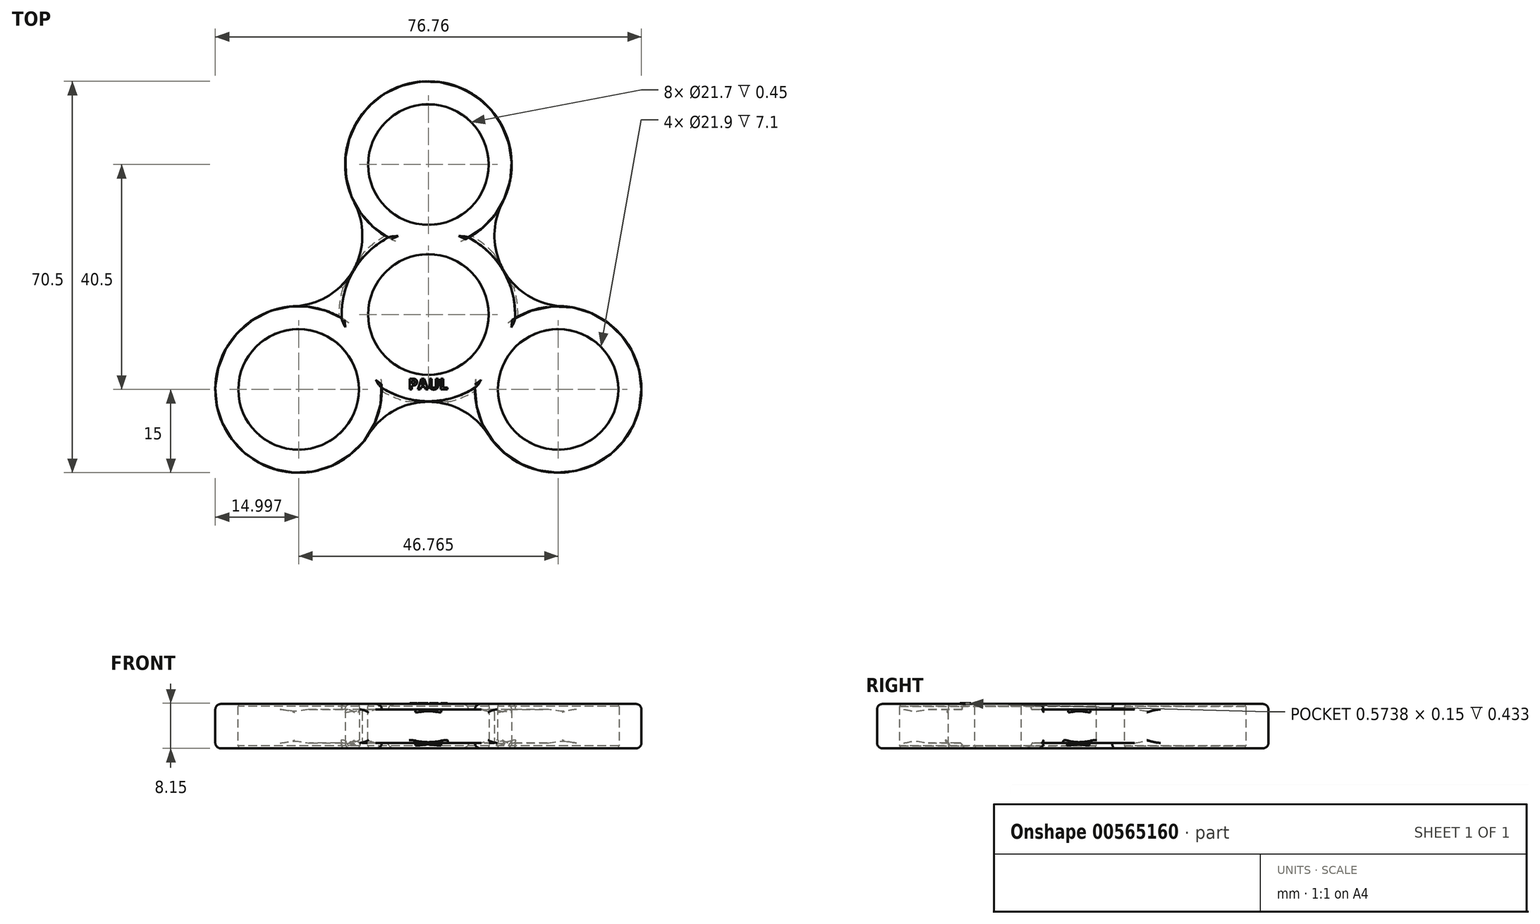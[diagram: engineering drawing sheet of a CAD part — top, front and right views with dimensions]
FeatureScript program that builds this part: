
annotation { "Feature Type Name" : "Feature", "Feature Type Description" : "" }
export const myFeature = defineFeature(function(context is Context, id is Id, definition is map)
    precondition{}
    {
        {
            var Q0;
            Q0=qCreatedBy(makeId("Top.planeOp"),FACE);
            var sketch = newSketch(context, id + "F0", { "sketchPlane" : qUnion([Q0])});
            skCircle(sketch, "E0", {"center": v(0, 0) * mm, "radius": 10.85 * mm});
            skCircle(sketch, "E1", {"center": v(0, 27) * mm, "radius": 10.85 * mm});
            skCircle(sketch, "E2.1.0", {"center": v(-23.38, -13.5) * mm, "radius": 10.85 * mm});
            skCircle(sketch, "E2.2.0", {"center": v(23.38, -13.5) * mm, "radius": 10.85 * mm});
            skArc(sketch, "E3", {"start": v(7.22, 13.85) * mm, "mid": v(0, 42) * mm, "end": v(-7.22, 13.85) * mm});
            skArc(sketch, "E4.1.0", {"start": v(8.39, -13.18) * mm, "mid": v(36.37, -21) * mm, "end": v(15.61, -0.67) * mm});
            skArc(sketch, "E4.2.0", {"start": v(-15.61, -0.67) * mm, "mid": v(-36.37, -21) * mm, "end": v(-8.39, -13.18) * mm});
            skArc(sketch, "E5", {"start": v(-8.39, -13.18) * mm, "mid": v(0, -15.62) * mm, "end": v(8.39, -13.18) * mm});
            skArc(sketch, "E6", {"start": v(-24.08, 1.48) * mm, "mid": v(-13.61, 7.86) * mm, "end": v(-13.33, 20.12) * mm});
            skArc(sketch, "E7", {"start": v(10.76, -21.6) * mm, "mid": v(0, -15.72) * mm, "end": v(-10.76, -21.6) * mm});
            skArc(sketch, "E8", {"start": v(13.33, 20.12) * mm, "mid": v(13.61, 7.86) * mm, "end": v(24.08, 1.48) * mm});
            skPoint(sketch, "E9.orphan", {"position": v(-13, 34.5) * mm});
            skPoint(sketch, "E10.orphan", {"position": v(-36.37, -6) * mm});
            skPoint(sketch, "E11.orphan", {"position": v(13, 34.5) * mm});
            skPoint(sketch, "E12.2.0.start.orphan", {"position": v(36.37, -6) * mm});
            skPoint(sketch, "E13.orphan", {"position": v(23.38, -28.5) * mm});
            skPoint(sketch, "E12.1.0.start.orphan", {"position": v(-23.38, -28.5) * mm});
            skArc(sketch, "E14.trimOffspring", {"start": v(15.61, -0.67) * mm, "mid": v(13.53, 7.81) * mm, "end": v(7.22, 13.85) * mm});
            skArc(sketch, "E15.trimOffspring", {"start": v(-7.22, 13.85) * mm, "mid": v(-13.53, 7.81) * mm, "end": v(-15.61, -0.67) * mm});
            skCircle(sketch, "E16", {"center": v(23.38, -13.5) * mm, "radius": 10.95 * mm});
            skCircle(sketch, "E17", {"center": v(-23.38, -13.5) * mm, "radius": 10.95 * mm});
            skCircle(sketch, "E18", {"center": v(0, 0) * mm, "radius": 10.95 * mm});
            skCircle(sketch, "E19", {"center": v(0, 27) * mm, "radius": 10.95 * mm});
            skSolve(sketch);
        }
        {
            var Q0;
            Q0=makeQuery(id+"F0.imprint","IMPRINT",FACE,{"disambiguationData":[TD([[makeQuery(id+"F0.imprint","IMPRINT",EDGE,{"derivedFrom":sQuery(id+"F0.wireOp",EDGE,"E2.1.0")}),-1.0]])]});
            var Q1;
            Q1=makeQuery(id+"F0.imprint","IMPRINT",FACE,{"disambiguationData":[TD([[makeQuery(id+"F0.imprint","IMPRINT",EDGE,{"derivedFrom":sQuery(id+"F0.wireOp",EDGE,"E0")}),-1.0]])]});
            var Q2;
            Q2=makeQuery(id+"F0.imprint","IMPRINT",FACE,{"disambiguationData":[TD([[makeQuery(id+"F0.imprint","IMPRINT",EDGE,{"derivedFrom":sQuery(id+"F0.wireOp",EDGE,"E1")}),-1.0]])]});
            var Q3;
            {var subQ0=sQuery(id+"F0.wireOp",EDGE,"E3");var subQ1=sQuery(id+"F0.wireOp",EDGE,"KJlQqC9l-gusD-toYh-YzLE-zyJcLNbmcpUm");var subQ2=makeQuery(id+"F0.imprint","INTERSECT",VERTEX,{"derivedFrom":[subQ1,subQ0]});Q3=makeQuery(id+"F0.imprint","IMPRINT",FACE,{"disambiguationData":[TD([[makeQuery(id+"F0.imprint","IMPRINT",EDGE,{"disambiguationData":[TD([[subQ2,1.0]])],"derivedFrom":subQ1}),1.0]])]});}
            var Q4;
            {var subQ0=sQuery(id+"F0.wireOp",EDGE,"E3");var subQ1=sQuery(id+"F0.wireOp",EDGE,"KJlQqC9l-gusD-toYh-YzLE-zyJcLNbmcpUm");var subQ2=makeQuery(id+"F0.imprint","INTERSECT",VERTEX,{"derivedFrom":[subQ1,subQ0]});Q4=makeQuery(id+"F0.imprint","IMPRINT",FACE,{"disambiguationData":[TD([[makeQuery(id+"F0.imprint","IMPRINT",EDGE,{"disambiguationData":[TD([[subQ2,1.0]])],"derivedFrom":subQ1}),-1.0]])]});}
            var Q5;
            {var subQ0=sQuery(id+"F0.wireOp",EDGE,"E5");var subQ1=sQuery(id+"F0.wireOp",EDGE,"E4.2.0");var subQ2=makeQuery(id+"F0.imprint","INTERSECT",VERTEX,{"disambiguationData":[OD(0.0)],"derivedFrom":[subQ1,subQ0]});Q5=makeQuery(id+"F0.imprint","IMPRINT",FACE,{"disambiguationData":[TD([[makeQuery(id+"F0.imprint","IMPRINT",EDGE,{"disambiguationData":[TD([[subQ2,-1.0]])],"derivedFrom":subQ1}),1.0]])]});}
            var Q6;
            Q6=makeQuery(id+"F0.imprint","IMPRINT",FACE,{"disambiguationData":[TD([[makeQuery(id+"F0.imprint","IMPRINT",EDGE,{"derivedFrom":sQuery(id+"F0.wireOp",EDGE,"E2.2.0")}),-1.0]])]});
            var Q7;
            {var subQ0=sQuery(id+"F0.wireOp",EDGE,"E5");var subQ1=sQuery(id+"F0.wireOp",EDGE,"E4.1.0");var subQ2=makeQuery(id+"F0.imprint","INTERSECT",VERTEX,{"disambiguationData":[OD(0.0)],"derivedFrom":[subQ1,subQ0]});Q7=makeQuery(id+"F0.imprint","IMPRINT",FACE,{"disambiguationData":[TD([[makeQuery(id+"F0.imprint","IMPRINT",EDGE,{"disambiguationData":[TD([[subQ2,-1.0]])],"derivedFrom":subQ1}),1.0]])]});}
            extrude(context, id + "F1", {"entities" : qUnion([Q0, Q1, Q2, Q3, Q4, Q5, Q6, Q7]), "endBound" : BoundingType.SYMMETRIC, "depth" : 8 * mm, "offsetDistance" : 25 * mm});
        }
        {
            var Q0;
            {var subQ0=sQuery(id+"F0.wireOp",EDGE,"E7");Q0=makeQuery(id+"F0.imprint","IMPRINT",FACE,{"disambiguationData":[TD([[makeQuery(id+"F0.imprint","IMPRINT",EDGE,{"derivedFrom":subQ0}),-1.0]])]});}
            var Q1;
            {var subQ0=sQuery(id+"F0.wireOp",EDGE,"E6");Q1=makeQuery(id+"F0.imprint","IMPRINT",FACE,{"disambiguationData":[TD([[makeQuery(id+"F0.imprint","IMPRINT",EDGE,{"derivedFrom":subQ0}),-1.0]])]});}
            var Q2;
            {var subQ0=sQuery(id+"F0.wireOp",EDGE,"E8");Q2=makeQuery(id+"F0.imprint","IMPRINT",FACE,{"disambiguationData":[TD([[makeQuery(id+"F0.imprint","IMPRINT",EDGE,{"derivedFrom":subQ0}),-1.0]])]});}
            extrude(context, id + "F2", {"entities" : qUnion([Q0, Q1, Q2]), "operationType" : NewBodyOperationType.ADD, "endBound" : BoundingType.SYMMETRIC, "depth" : 6 * mm, "offsetDistance" : 25 * mm});
        }
        {
            var Q0;
            Q0=makeQuery(id+"F1.opExtrude","CAP_EDGE",EDGE,{"disambiguationData":[OSD([sQuery(id+"F0.wireOp",EDGE,"E15.trimOffspring")])],"isStart":true});
            var Q1;
            Q1=makeQuery(id+"F2.opExtrude","CAP_EDGE",EDGE,{"disambiguationData":[OSD([sQuery(id+"F0.wireOp",EDGE,"E15.trimOffspring")])],"isStart":true});
            var Q2;
            Q2=makeQuery(id+"F1.opExtrude","CAP_EDGE",EDGE,{"disambiguationData":[OSD([sQuery(id+"F0.wireOp",EDGE,"E5")])],"isStart":true});
            var Q3;
            Q3=makeQuery(id+"F2.opExtrude","CAP_EDGE",EDGE,{"disambiguationData":[OSD([sQuery(id+"F0.wireOp",EDGE,"E5")])],"isStart":true});
            var Q4;
            Q4=makeQuery(id+"F1.opExtrude","CAP_EDGE",EDGE,{"disambiguationData":[OSD([sQuery(id+"F0.wireOp",EDGE,"E14.trimOffspring")])],"isStart":true});
            var Q5;
            Q5=makeQuery(id+"F2.opExtrude","CAP_EDGE",EDGE,{"disambiguationData":[OSD([sQuery(id+"F0.wireOp",EDGE,"E14.trimOffspring")])],"isStart":true});
            fillet(context, id + "F3", {"entities" : qUnion([Q0, Q1, Q2, Q3, Q4, Q5]), "radius" : 0.5 * mm, "rho" : 0.5, "crossSection" : FilletCrossSection.CONIC, "allowEdgeOverflow" : false});
        }
        {
            var Q0;
            Q0=makeQuery(id+"F1.opExtrude","CAP_EDGE",EDGE,{"disambiguationData":[OSD([sQuery(id+"F0.wireOp",EDGE,"E5")])],"isStart":false});
            var Q1;
            Q1=makeQuery(id+"F2.opExtrude","CAP_EDGE",EDGE,{"disambiguationData":[OSD([sQuery(id+"F0.wireOp",EDGE,"E5")])],"isStart":false});
            var Q2;
            Q2=makeQuery(id+"F1.opExtrude","CAP_EDGE",EDGE,{"disambiguationData":[OSD([sQuery(id+"F0.wireOp",EDGE,"E14.trimOffspring")])],"isStart":false});
            var Q3;
            Q3=makeQuery(id+"F2.opExtrude","CAP_EDGE",EDGE,{"disambiguationData":[OSD([sQuery(id+"F0.wireOp",EDGE,"E14.trimOffspring")])],"isStart":false});
            var Q4;
            Q4=makeQuery(id+"F1.opExtrude","CAP_EDGE",EDGE,{"disambiguationData":[OSD([sQuery(id+"F0.wireOp",EDGE,"E15.trimOffspring")])],"isStart":false});
            var Q5;
            Q5=makeQuery(id+"F2.opExtrude","CAP_EDGE",EDGE,{"disambiguationData":[OSD([sQuery(id+"F0.wireOp",EDGE,"E15.trimOffspring")])],"isStart":false});
            fillet(context, id + "F4", {"entities" : qUnion([Q0, Q1, Q2, Q3, Q4, Q5]), "radius" : 0.5 * mm, "rho" : 0.5, "crossSection" : FilletCrossSection.CONIC, "allowEdgeOverflow" : false});
        }
        {
            var Q0;
            Q0=makeQuery(id+"F1.opExtrude","CAP_EDGE",EDGE,{"disambiguationData":[OSD([sQuery(id+"F0.wireOp",EDGE,"E4.1.0")])],"isStart":false});
            var Q1;
            Q1=makeQuery(id+"F1.opExtrude","CAP_EDGE",EDGE,{"disambiguationData":[OSD([sQuery(id+"F0.wireOp",EDGE,"E3")])],"isStart":false});
            var Q2;
            Q2=makeQuery(id+"F1.opExtrude","CAP_EDGE",EDGE,{"disambiguationData":[OSD([sQuery(id+"F0.wireOp",EDGE,"E4.2.0")])],"isStart":false});
            var Q3;
            Q3=makeQuery(id+"F1.opExtrude","CAP_EDGE",EDGE,{"disambiguationData":[OSD([sQuery(id+"F0.wireOp",EDGE,"E4.2.0")])],"isStart":true});
            var Q4;
            Q4=makeQuery(id+"F1.opExtrude","CAP_EDGE",EDGE,{"disambiguationData":[OSD([sQuery(id+"F0.wireOp",EDGE,"E4.1.0")])],"isStart":true});
            var Q5;
            Q5=makeQuery(id+"F1.opExtrude","CAP_EDGE",EDGE,{"disambiguationData":[OSD([sQuery(id+"F0.wireOp",EDGE,"E3")])],"isStart":true});
            fillet(context, id + "F5", {"entities" : qUnion([Q0, Q1, Q2, Q3, Q4, Q5]), "radius" : 1 * mm, "allowEdgeOverflow" : false});
        }
        {
            var Q0;
            Q0=makeQuery(id+"F2.opExtrude","SWEPT_FACE",FACE,{"disambiguationData":[OSD([sQuery(id+"F0.wireOp",EDGE,"E8")])]});
            var Q1;
            Q1=makeQuery(id+"F2.opExtrude","SWEPT_FACE",FACE,{"disambiguationData":[OSD([sQuery(id+"F0.wireOp",EDGE,"E6")])]});
            var Q2;
            Q2=makeQuery(id+"F2.opExtrude","SWEPT_FACE",FACE,{"disambiguationData":[OSD([sQuery(id+"F0.wireOp",EDGE,"E7")])]});
            fillet(context, id + "F6", {"entities" : qUnion([Q0, Q1, Q2]), "radius" : .5 * mm, "tangentPropagation" : true, "allowEdgeOverflow" : false});
        }
        {
            var Q0;
            Q0=makeQuery(id+"F0.imprint","IMPRINT",FACE,{"disambiguationData":[TD([[makeQuery(id+"F0.imprint","IMPRINT",EDGE,{"derivedFrom":sQuery(id+"F0.wireOp",EDGE,"E19")}),1.0]])]});
            var Q1;
            Q1=makeQuery(id+"F0.imprint","IMPRINT",FACE,{"disambiguationData":[TD([[makeQuery(id+"F0.imprint","IMPRINT",EDGE,{"derivedFrom":sQuery(id+"F0.wireOp",EDGE,"E18")}),1.0]])]});
            var Q2;
            Q2=makeQuery(id+"F0.imprint","IMPRINT",FACE,{"disambiguationData":[TD([[makeQuery(id+"F0.imprint","IMPRINT",EDGE,{"derivedFrom":sQuery(id+"F0.wireOp",EDGE,"E16")}),1.0]])]});
            var Q3;
            Q3=makeQuery(id+"F0.imprint","IMPRINT",FACE,{"disambiguationData":[TD([[makeQuery(id+"F0.imprint","IMPRINT",EDGE,{"derivedFrom":sQuery(id+"F0.wireOp",EDGE,"E17")}),1.0]])]});
            extrude(context, id + "F7", {"entities" : qUnion([Q0, Q1, Q2, Q3]), "endBound" : BoundingType.SYMMETRIC, "depth" : 7.1 * mm, "offsetDistance" : 25 * mm});
        }
        {
            var Q0;
            Q0=makeQuery(id+"F7.opExtrude","SWEPT_BODY",BODY,{"disambiguationData":[OSD([sQuery(id+"F0.wireOp",EDGE,"E16")])]});
            var Q1;
            Q1=makeQuery(id+"F7.opExtrude","SWEPT_BODY",BODY,{"disambiguationData":[OSD([sQuery(id+"F0.wireOp",EDGE,"E17")])]});
            var Q2;
            Q2=makeQuery(id+"F7.opExtrude","SWEPT_BODY",BODY,{"disambiguationData":[OSD([sQuery(id+"F0.wireOp",EDGE,"E18")])]});
            var Q3;
            Q3=makeQuery(id+"F7.opExtrude","SWEPT_BODY",BODY,{"disambiguationData":[OSD([sQuery(id+"F0.wireOp",EDGE,"E19")])]});
            var Q4;
            Q4=makeQuery(id+"F1.opExtrude","SWEPT_BODY",BODY,{"disambiguationData":[OSD([sQuery(id+"F0.wireOp",EDGE,"E0"),sQuery(id+"F0.wireOp",EDGE,"E1"),sQuery(id+"F0.wireOp",EDGE,"E2.1.0"),sQuery(id+"F0.wireOp",EDGE,"E2.2.0"),sQuery(id+"F0.wireOp",EDGE,"E3"),sQuery(id+"F0.wireOp",EDGE,"E4.1.0"),sQuery(id+"F0.wireOp",EDGE,"E4.2.0"),sQuery(id+"F0.wireOp",EDGE,"E5"),sQuery(id+"F0.wireOp",EDGE,"E14.trimOffspring"),sQuery(id+"F0.wireOp",EDGE,"E15.trimOffspring"),sQuery(id+"F0.wireOp",EDGE,"f471b002-4030-4226-8843-a168e7eb6244.sketch_text.stroke-7"),sQuery(id+"F0.wireOp",EDGE,"f471b002-4030-4226-8843-a168e7eb6244.sketch_text.stroke-8"),sQuery(id+"F0.wireOp",EDGE,"f471b002-4030-4226-8843-a168e7eb6244.sketch_text.stroke-9"),sQuery(id+"F0.wireOp",EDGE,"f471b002-4030-4226-8843-a168e7eb6244.sketch_text.stroke-10"),sQuery(id+"F0.wireOp",EDGE,"f471b002-4030-4226-8843-a168e7eb6244.sketch_text.stroke-11"),sQuery(id+"F0.wireOp",EDGE,"f471b002-4030-4226-8843-a168e7eb6244.sketch_text.stroke-12"),sQuery(id+"F0.wireOp",EDGE,"f471b002-4030-4226-8843-a168e7eb6244.sketch_text.stroke-13"),sQuery(id+"F0.wireOp",EDGE,"f471b002-4030-4226-8843-a168e7eb6244.sketch_text.stroke-14"),sQuery(id+"F0.wireOp",EDGE,"f471b002-4030-4226-8843-a168e7eb6244.sketch_text.stroke-15"),sQuery(id+"F0.wireOp",EDGE,"f471b002-4030-4226-8843-a168e7eb6244.sketch_text.stroke-16"),sQuery(id+"F0.wireOp",EDGE,"f471b002-4030-4226-8843-a168e7eb6244.sketch_text.stroke-17"),sQuery(id+"F0.wireOp",EDGE,"f471b002-4030-4226-8843-a168e7eb6244.sketch_text.stroke-18"),sQuery(id+"F0.wireOp",EDGE,"f471b002-4030-4226-8843-a168e7eb6244.sketch_text.stroke-19"),sQuery(id+"F0.wireOp",EDGE,"f471b002-4030-4226-8843-a168e7eb6244.sketch_text.stroke-20"),sQuery(id+"F0.wireOp",EDGE,"f471b002-4030-4226-8843-a168e7eb6244.sketch_text.stroke-21"),sQuery(id+"F0.wireOp",EDGE,"f471b002-4030-4226-8843-a168e7eb6244.sketch_text.stroke-22"),sQuery(id+"F0.wireOp",EDGE,"f471b002-4030-4226-8843-a168e7eb6244.sketch_text.stroke-23"),sQuery(id+"F0.wireOp",EDGE,"f471b002-4030-4226-8843-a168e7eb6244.sketch_text.stroke-28"),sQuery(id+"F0.wireOp",EDGE,"f471b002-4030-4226-8843-a168e7eb6244.sketch_text.stroke-29"),sQuery(id+"F0.wireOp",EDGE,"f471b002-4030-4226-8843-a168e7eb6244.sketch_text.stroke-30"),sQuery(id+"F0.wireOp",EDGE,"f471b002-4030-4226-8843-a168e7eb6244.sketch_text.stroke-31"),sQuery(id+"F0.wireOp",EDGE,"f471b002-4030-4226-8843-a168e7eb6244.sketch_text.stroke-32"),sQuery(id+"F0.wireOp",EDGE,"f471b002-4030-4226-8843-a168e7eb6244.sketch_text.stroke-33"),sQuery(id+"F0.wireOp",EDGE,"f471b002-4030-4226-8843-a168e7eb6244.sketch_text.stroke-34"),sQuery(id+"F0.wireOp",EDGE,"f471b002-4030-4226-8843-a168e7eb6244.sketch_text.stroke-35"),sQuery(id+"F0.wireOp",EDGE,"f471b002-4030-4226-8843-a168e7eb6244.sketch_text.stroke-36"),sQuery(id+"F0.wireOp",EDGE,"f471b002-4030-4226-8843-a168e7eb6244.sketch_text.stroke-37"),sQuery(id+"F0.wireOp",EDGE,"f471b002-4030-4226-8843-a168e7eb6244.sketch_text.stroke-38"),sQuery(id+"F0.wireOp",EDGE,"f471b002-4030-4226-8843-a168e7eb6244.sketch_text.stroke-39"),sQuery(id+"F0.wireOp",EDGE,"f471b002-4030-4226-8843-a168e7eb6244.sketch_text.stroke-40"),sQuery(id+"F0.wireOp",EDGE,"f471b002-4030-4226-8843-a168e7eb6244.sketch_text.stroke-41"),sQuery(id+"F0.wireOp",EDGE,"f471b002-4030-4226-8843-a168e7eb6244.sketch_text.stroke-42"),sQuery(id+"F0.wireOp",EDGE,"f471b002-4030-4226-8843-a168e7eb6244.sketch_text.stroke-43"),sQuery(id+"F0.wireOp",EDGE,"f471b002-4030-4226-8843-a168e7eb6244.sketch_text.stroke-44"),sQuery(id+"F0.wireOp",EDGE,"f471b002-4030-4226-8843-a168e7eb6244.sketch_text.stroke-45"),sQuery(id+"F0.wireOp",EDGE,"f471b002-4030-4226-8843-a168e7eb6244.sketch_text.stroke-46"),sQuery(id+"F0.wireOp",EDGE,"f471b002-4030-4226-8843-a168e7eb6244.sketch_text.stroke-47"),sQuery(id+"F0.wireOp",EDGE,"f471b002-4030-4226-8843-a168e7eb6244.sketch_text.stroke-48"),sQuery(id+"F0.wireOp",EDGE,"f471b002-4030-4226-8843-a168e7eb6244.sketch_text.stroke-49"),sQuery(id+"F0.wireOp",EDGE,"f471b002-4030-4226-8843-a168e7eb6244.sketch_text.stroke-50"),sQuery(id+"F0.wireOp",EDGE,"f471b002-4030-4226-8843-a168e7eb6244.sketch_text.stroke-51"),sQuery(id+"F0.wireOp",EDGE,"f471b002-4030-4226-8843-a168e7eb6244.sketch_text.stroke-52"),sQuery(id+"F0.wireOp",EDGE,"f471b002-4030-4226-8843-a168e7eb6244.sketch_text.stroke-53"),sQuery(id+"F0.wireOp",EDGE,"f471b002-4030-4226-8843-a168e7eb6244.sketch_text.stroke-54"),sQuery(id+"F0.wireOp",EDGE,"f471b002-4030-4226-8843-a168e7eb6244.sketch_text.stroke-55"),sQuery(id+"F0.wireOp",EDGE,"f471b002-4030-4226-8843-a168e7eb6244.sketch_text.stroke-56"),sQuery(id+"F0.wireOp",EDGE,"f471b002-4030-4226-8843-a168e7eb6244.sketch_text.stroke-57"),sQuery(id+"F0.wireOp",EDGE,"f471b002-4030-4226-8843-a168e7eb6244.sketch_text.stroke-58"),sQuery(id+"F0.wireOp",EDGE,"f471b002-4030-4226-8843-a168e7eb6244.sketch_text.stroke-59"),sQuery(id+"F0.wireOp",EDGE,"f471b002-4030-4226-8843-a168e7eb6244.sketch_text.stroke-60"),sQuery(id+"F0.wireOp",EDGE,"f471b002-4030-4226-8843-a168e7eb6244.sketch_text.stroke-74"),sQuery(id+"F0.wireOp",EDGE,"f471b002-4030-4226-8843-a168e7eb6244.sketch_text.stroke-75"),sQuery(id+"F0.wireOp",EDGE,"f471b002-4030-4226-8843-a168e7eb6244.sketch_text.stroke-76"),sQuery(id+"F0.wireOp",EDGE,"f471b002-4030-4226-8843-a168e7eb6244.sketch_text.stroke-77"),sQuery(id+"F0.wireOp",EDGE,"f471b002-4030-4226-8843-a168e7eb6244.sketch_text.stroke-78"),sQuery(id+"F0.wireOp",EDGE,"f471b002-4030-4226-8843-a168e7eb6244.sketch_text.stroke-79"),sQuery(id+"F0.wireOp",EDGE,"f471b002-4030-4226-8843-a168e7eb6244.sketch_text.stroke-80"),sQuery(id+"F0.wireOp",EDGE,"f471b002-4030-4226-8843-a168e7eb6244.sketch_text.stroke-81"),sQuery(id+"F0.wireOp",EDGE,"f471b002-4030-4226-8843-a168e7eb6244.sketch_text.stroke-86"),sQuery(id+"F0.wireOp",EDGE,"f471b002-4030-4226-8843-a168e7eb6244.sketch_text.stroke-87"),sQuery(id+"F0.wireOp",EDGE,"f471b002-4030-4226-8843-a168e7eb6244.sketch_text.stroke-88"),sQuery(id+"F0.wireOp",EDGE,"f471b002-4030-4226-8843-a168e7eb6244.sketch_text.stroke-89"),sQuery(id+"F0.wireOp",EDGE,"f471b002-4030-4226-8843-a168e7eb6244.sketch_text.stroke-90"),sQuery(id+"F0.wireOp",EDGE,"f471b002-4030-4226-8843-a168e7eb6244.sketch_text.stroke-91"),sQuery(id+"F0.wireOp",EDGE,"f471b002-4030-4226-8843-a168e7eb6244.sketch_text.stroke-92"),sQuery(id+"F0.wireOp",EDGE,"f471b002-4030-4226-8843-a168e7eb6244.sketch_text.stroke-93"),sQuery(id+"F0.wireOp",EDGE,"f471b002-4030-4226-8843-a168e7eb6244.sketch_text.stroke-94"),sQuery(id+"F0.wireOp",EDGE,"f471b002-4030-4226-8843-a168e7eb6244.sketch_text.stroke-95"),sQuery(id+"F0.wireOp",EDGE,"f471b002-4030-4226-8843-a168e7eb6244.sketch_text.stroke-96"),sQuery(id+"F0.wireOp",EDGE,"f471b002-4030-4226-8843-a168e7eb6244.sketch_text.stroke-97"),sQuery(id+"F0.wireOp",EDGE,"f471b002-4030-4226-8843-a168e7eb6244.sketch_text.stroke-98"),sQuery(id+"F0.wireOp",EDGE,"f471b002-4030-4226-8843-a168e7eb6244.sketch_text.stroke-99"),sQuery(id+"F0.wireOp",EDGE,"f471b002-4030-4226-8843-a168e7eb6244.sketch_text.stroke-100"),sQuery(id+"F0.wireOp",EDGE,"f471b002-4030-4226-8843-a168e7eb6244.sketch_text.stroke-101"),sQuery(id+"F0.wireOp",EDGE,"f471b002-4030-4226-8843-a168e7eb6244.sketch_text.stroke-102"),sQuery(id+"F0.wireOp",EDGE,"f471b002-4030-4226-8843-a168e7eb6244.sketch_text.stroke-103"),sQuery(id+"F0.wireOp",EDGE,"f471b002-4030-4226-8843-a168e7eb6244.sketch_text.stroke-104"),sQuery(id+"F0.wireOp",EDGE,"f471b002-4030-4226-8843-a168e7eb6244.sketch_text.stroke-105"),sQuery(id+"F0.wireOp",EDGE,"f471b002-4030-4226-8843-a168e7eb6244.sketch_text.stroke-106"),sQuery(id+"F0.wireOp",EDGE,"f471b002-4030-4226-8843-a168e7eb6244.sketch_text.stroke-107"),sQuery(id+"F0.wireOp",EDGE,"f471b002-4030-4226-8843-a168e7eb6244.sketch_text.stroke-108"),sQuery(id+"F0.wireOp",EDGE,"f471b002-4030-4226-8843-a168e7eb6244.sketch_text.stroke-109"),sQuery(id+"F0.wireOp",EDGE,"f471b002-4030-4226-8843-a168e7eb6244.sketch_text.stroke-110"),sQuery(id+"F0.wireOp",EDGE,"f471b002-4030-4226-8843-a168e7eb6244.sketch_text.stroke-111"),sQuery(id+"F0.wireOp",EDGE,"f471b002-4030-4226-8843-a168e7eb6244.sketch_text.stroke-112"),sQuery(id+"F0.wireOp",EDGE,"f471b002-4030-4226-8843-a168e7eb6244.sketch_text.stroke-113"),sQuery(id+"F0.wireOp",EDGE,"f471b002-4030-4226-8843-a168e7eb6244.sketch_text.stroke-114"),sQuery(id+"F0.wireOp",EDGE,"f471b002-4030-4226-8843-a168e7eb6244.sketch_text.stroke-115"),sQuery(id+"F0.wireOp",EDGE,"f471b002-4030-4226-8843-a168e7eb6244.sketch_text.stroke-116"),sQuery(id+"F0.wireOp",EDGE,"f471b002-4030-4226-8843-a168e7eb6244.sketch_text.stroke-117"),sQuery(id+"F0.wireOp",EDGE,"f471b002-4030-4226-8843-a168e7eb6244.sketch_text.stroke-118"),sQuery(id+"F0.wireOp",EDGE,"f471b002-4030-4226-8843-a168e7eb6244.sketch_text.stroke-119"),sQuery(id+"F0.wireOp",EDGE,"f471b002-4030-4226-8843-a168e7eb6244.sketch_text.stroke-120"),sQuery(id+"F0.wireOp",EDGE,"f471b002-4030-4226-8843-a168e7eb6244.sketch_text.stroke-121"),sQuery(id+"F0.wireOp",EDGE,"f471b002-4030-4226-8843-a168e7eb6244.sketch_text.stroke-122"),sQuery(id+"F0.wireOp",EDGE,"f471b002-4030-4226-8843-a168e7eb6244.sketch_text.stroke-123"),sQuery(id+"F0.wireOp",EDGE,"f471b002-4030-4226-8843-a168e7eb6244.sketch_text.stroke-124"),sQuery(id+"F0.wireOp",EDGE,"f471b002-4030-4226-8843-a168e7eb6244.sketch_text.stroke-125"),sQuery(id+"F0.wireOp",EDGE,"f471b002-4030-4226-8843-a168e7eb6244.sketch_text.stroke-126"),sQuery(id+"F0.wireOp",EDGE,"f471b002-4030-4226-8843-a168e7eb6244.sketch_text.stroke-127"),sQuery(id+"F0.wireOp",EDGE,"f471b002-4030-4226-8843-a168e7eb6244.sketch_text.stroke-128"),sQuery(id+"F0.wireOp",EDGE,"f471b002-4030-4226-8843-a168e7eb6244.sketch_text.stroke-129"),sQuery(id+"F0.wireOp",EDGE,"f471b002-4030-4226-8843-a168e7eb6244.sketch_text.stroke-130"),sQuery(id+"F0.wireOp",EDGE,"f471b002-4030-4226-8843-a168e7eb6244.sketch_text.stroke-131"),sQuery(id+"F0.wireOp",EDGE,"f471b002-4030-4226-8843-a168e7eb6244.sketch_text.stroke-132"),sQuery(id+"F0.wireOp",EDGE,"f471b002-4030-4226-8843-a168e7eb6244.sketch_text.stroke-133"),sQuery(id+"F0.wireOp",EDGE,"f471b002-4030-4226-8843-a168e7eb6244.sketch_text.stroke-134"),sQuery(id+"F0.wireOp",EDGE,"f471b002-4030-4226-8843-a168e7eb6244.sketch_text.stroke-135"),sQuery(id+"F0.wireOp",EDGE,"f471b002-4030-4226-8843-a168e7eb6244.sketch_text.stroke-136"),sQuery(id+"F0.wireOp",EDGE,"f471b002-4030-4226-8843-a168e7eb6244.sketch_text.stroke-137"),sQuery(id+"F0.wireOp",EDGE,"f471b002-4030-4226-8843-a168e7eb6244.sketch_text.stroke-138"),sQuery(id+"F0.wireOp",EDGE,"f471b002-4030-4226-8843-a168e7eb6244.sketch_text.stroke-139"),sQuery(id+"F0.wireOp",EDGE,"f471b002-4030-4226-8843-a168e7eb6244.sketch_text.stroke-140"),sQuery(id+"F0.wireOp",EDGE,"f471b002-4030-4226-8843-a168e7eb6244.sketch_text.stroke-141"),sQuery(id+"F0.wireOp",EDGE,"f471b002-4030-4226-8843-a168e7eb6244.sketch_text.stroke-142"),sQuery(id+"F0.wireOp",EDGE,"f471b002-4030-4226-8843-a168e7eb6244.sketch_text.stroke-143"),sQuery(id+"F0.wireOp",EDGE,"f471b002-4030-4226-8843-a168e7eb6244.sketch_text.stroke-144"),sQuery(id+"F0.wireOp",EDGE,"f471b002-4030-4226-8843-a168e7eb6244.sketch_text.stroke-145"),sQuery(id+"F0.wireOp",EDGE,"f471b002-4030-4226-8843-a168e7eb6244.sketch_text.stroke-146"),sQuery(id+"F0.wireOp",EDGE,"f471b002-4030-4226-8843-a168e7eb6244.sketch_text.stroke-147"),sQuery(id+"F0.wireOp",EDGE,"f471b002-4030-4226-8843-a168e7eb6244.sketch_text.stroke-148"),sQuery(id+"F0.wireOp",EDGE,"f471b002-4030-4226-8843-a168e7eb6244.sketch_text.stroke-149"),sQuery(id+"F0.wireOp",EDGE,"f471b002-4030-4226-8843-a168e7eb6244.sketch_text.stroke-150"),sQuery(id+"F0.wireOp",EDGE,"f471b002-4030-4226-8843-a168e7eb6244.sketch_text.stroke-151"),sQuery(id+"F0.wireOp",EDGE,"f471b002-4030-4226-8843-a168e7eb6244.sketch_text.stroke-152"),sQuery(id+"F0.wireOp",EDGE,"f471b002-4030-4226-8843-a168e7eb6244.sketch_text.stroke-153"),sQuery(id+"F0.wireOp",EDGE,"f471b002-4030-4226-8843-a168e7eb6244.sketch_text.stroke-154"),sQuery(id+"F0.wireOp",EDGE,"f471b002-4030-4226-8843-a168e7eb6244.sketch_text.stroke-155"),sQuery(id+"F0.wireOp",EDGE,"f471b002-4030-4226-8843-a168e7eb6244.sketch_text.stroke-156"),sQuery(id+"F0.wireOp",EDGE,"f471b002-4030-4226-8843-a168e7eb6244.sketch_text.stroke-157"),sQuery(id+"F0.wireOp",EDGE,"f471b002-4030-4226-8843-a168e7eb6244.sketch_text.stroke-158"),sQuery(id+"F0.wireOp",EDGE,"f471b002-4030-4226-8843-a168e7eb6244.sketch_text.stroke-159"),sQuery(id+"F0.wireOp",EDGE,"f471b002-4030-4226-8843-a168e7eb6244.sketch_text.stroke-160"),sQuery(id+"F0.wireOp",EDGE,"f471b002-4030-4226-8843-a168e7eb6244.sketch_text.stroke-161"),sQuery(id+"F0.wireOp",EDGE,"f471b002-4030-4226-8843-a168e7eb6244.sketch_text.stroke-162"),sQuery(id+"F0.wireOp",EDGE,"f471b002-4030-4226-8843-a168e7eb6244.sketch_text.stroke-163"),sQuery(id+"F0.wireOp",EDGE,"f471b002-4030-4226-8843-a168e7eb6244.sketch_text.stroke-164"),sQuery(id+"F0.wireOp",EDGE,"f471b002-4030-4226-8843-a168e7eb6244.sketch_text.stroke-165"),sQuery(id+"F0.wireOp",EDGE,"f471b002-4030-4226-8843-a168e7eb6244.sketch_text.stroke-166"),sQuery(id+"F0.wireOp",EDGE,"f471b002-4030-4226-8843-a168e7eb6244.sketch_text.stroke-167"),sQuery(id+"F0.wireOp",EDGE,"f471b002-4030-4226-8843-a168e7eb6244.sketch_text.stroke-168"),sQuery(id+"F0.wireOp",EDGE,"f471b002-4030-4226-8843-a168e7eb6244.sketch_text.stroke-169"),sQuery(id+"F0.wireOp",EDGE,"f471b002-4030-4226-8843-a168e7eb6244.sketch_text.stroke-170")])]});
            booleanBodies(context, id + "F8", {"operationType" : BooleanOperationType.SUBTRACTION, "tools" : qUnion([Q0, Q1, Q2, Q3]), "targets" : qUnion([Q4])});
        }
        {
            var Q0;
            Q0=makeQuery(id+"F1.opExtrude","CAP_FACE",FACE,{"disambiguationData":[OSD([sQuery(id+"F0.wireOp",EDGE,"E0"),sQuery(id+"F0.wireOp",EDGE,"E1"),sQuery(id+"F0.wireOp",EDGE,"E2.1.0"),sQuery(id+"F0.wireOp",EDGE,"E2.2.0"),sQuery(id+"F0.wireOp",EDGE,"E3"),sQuery(id+"F0.wireOp",EDGE,"E4.1.0"),sQuery(id+"F0.wireOp",EDGE,"E4.2.0"),sQuery(id+"F0.wireOp",EDGE,"E5"),sQuery(id+"F0.wireOp",EDGE,"E14.trimOffspring"),sQuery(id+"F0.wireOp",EDGE,"E15.trimOffspring")])],"isStart":false});
            var sketch = newSketch(context, id + "F9", { "sketchPlane" : qUnion([Q0])});
            skText(sketch, "E20", { "text": "PAUL", "fontName": "OpenSans-Bold.ttf"});
            skLineSegment(sketch, "E21", {"start": v(0, 0) * mm, "end": v(0, -20.78) * mm});
            const initialGuessF9  = {"E20": [-0.00362, -0.0135, 1, 0, 0.00195]};
            skSetInitialGuess(sketch, initialGuessF9);
            skSolve(sketch);
        }
        {
            var Q0;
            Q0=qSketchRegion(id+"F9",true);
            extrude(context, id + "F10", {"entities" : qUnion([Q0]), "operationType" : NewBodyOperationType.ADD, "depth" : .15 * mm, "offsetDistance" : 25 * mm});
        }
    });
